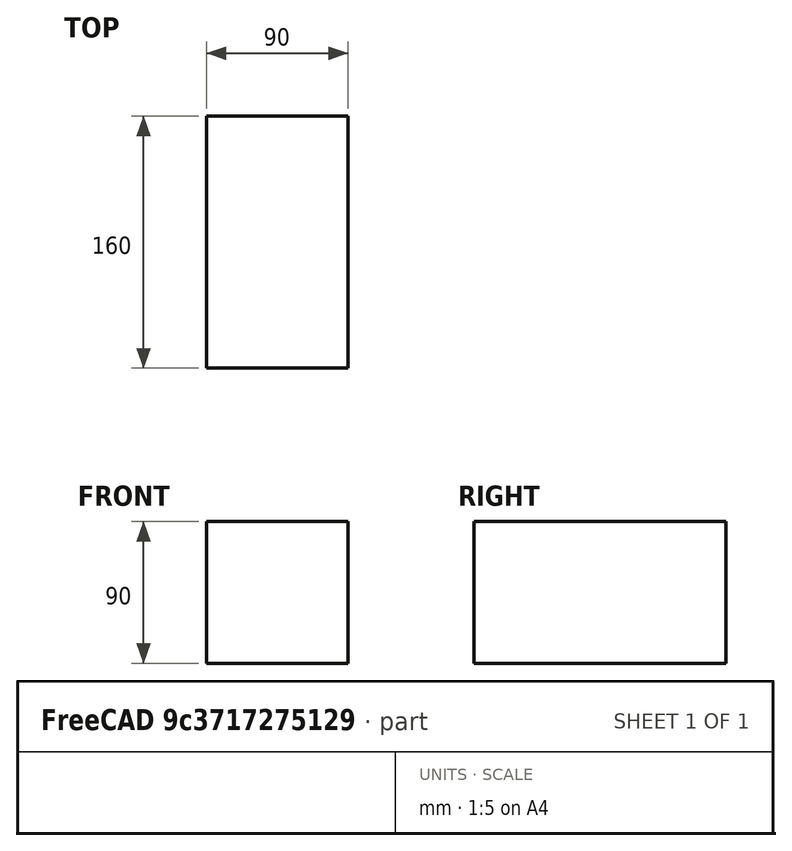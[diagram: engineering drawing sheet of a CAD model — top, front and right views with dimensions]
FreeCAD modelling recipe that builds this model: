
FCSTD DOCUMENT  (FreeCAD 0.18R4 (GitTag))
Label: Box-A
License: All rights reserved
LicenseURL: http://en.wikipedia.org/wiki/All_rights_reserved
objects: Sketcher::SketchObject×1, PartDesign::Pad×1, PartDesign::Body×1
note: 4 computed .brp shape members not serialized (recipe doc carries the construction recipe); baked Part::Feature solids carry a one-line shape summary decoded from their .brp

FEATURE [Sketcher::SketchObject] Sketch
  MapMode = 5
  Support = -> [XY_Plane]
  sketch-geometry (4):
    g0: LineSegment StartX=0 StartY=0 StartZ=0 EndX=-90 EndY=0 EndZ=0
    g1: LineSegment StartX=-90 StartY=0 StartZ=0 EndX=-90 EndY=160 EndZ=0
    g2: LineSegment StartX=-90 StartY=160 StartZ=0 EndX=0 EndY=160 EndZ=0
    g3: LineSegment StartX=0 StartY=160 StartZ=0 EndX=0 EndY=0 EndZ=0
  constraints (10):
    c: Coincident(g0,g1)
    c: Coincident(g1,g2)
    c: Coincident(g2,g3)
    c: Coincident(g3,g0)
    c: Horizontal(g2)
    c: Vertical(g1)
    c: Distance(g0) = 90
    c: Distance(g1) = 160
    c: Tangent(g3,g-2)
    c: Tangent(g0,g-1)
FEATURE [PartDesign::Pad] Pad
  Length = 90
  Length2 = 100
  Profile = -> Sketch
  Type = 0
FEATURE [PartDesign::Body] Body
  Group = -> [Sketch,Pad]
  Origin = -> Origin
  Tip = -> Pad
